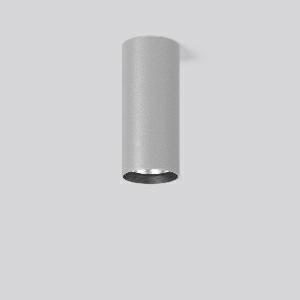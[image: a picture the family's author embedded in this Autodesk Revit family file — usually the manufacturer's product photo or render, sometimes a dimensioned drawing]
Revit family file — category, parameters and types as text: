
# Revit family: heledon_mini_a_931209_004_3_2080
name_source: partatom
category: Lighting Fixtures
units: mm (PartAtom-declared; Revit-internal decimal feet)

## family parameters
Cut with Voids When Loaded = No
Host = Face
Light Source = No
Part Type = Normal
Room Calculation Point = No
Round Connector Dimension = Use Diameter
Shared = No

## types (1)
- HELEDON mini A (1 x LED Modul 935, 3600 lm, 3500)
    Apparent Load = 29 VA
    Approval mark = CE
    CIE Flux Codes = 99 100 100 100 100
    Color Rendering = 92
    Color Temperature = 3500
    Default Elevation = 1800 mm
    Description = Series: HELEDON mini
Cylindrical surface-mounted downlight. Housing: die-cast aluminium, powder-coated. Internal ceiling frame polycarbonate with bayonet mounting. Black plastic ring and recessed LED to prevent glare from the side. Optical assembly with reflector made of MIRO-Silver with 98% total light reflection for outstanding efficiency - can be changed without tools. Best colour rendering index Ra>90. Suitable for Ceiling mounting. Easy installation with a separate ceiling frame with bayonet mounting and plug connection. Driver integrated. Connected via plug-in connector. High quality converter without flickering and stroboscopic effect. The following accessories can be mounted without use of tools: interchangeable lenses, decorative glasses, honeycomb louvre, clear and frosted diffusers, white interchangeable plastic ring. 
Colour: silver
Diameter: 87 mm
Height: 197 mm
Lamp: LED
Socket: without socket
Colour temperature: 3500K
Colour rendering index (CRI): 92
System power: 29 W
Rated luminous flux: 3600 lm
Luminous efficiency: 124 lm/W
Control gear: Regulated power supply
Protection class: I
Type of protection: IP 20
    Height = 197 mm
    Lamp = 1 x LED Modul 935
    Lamp Light Flux = 3600 lm
    Lamp count = 1
    Length = 87 mm
    Lifetime = 50000 h
    Luminous efficacy = 124 lm/W
    Manufacturer = RZB
    ModVariant = No
    Model = 931209.004.3
    Mounting Place = Ceiling
    Mounting Type = Surface mounted
    Number of Poles = 1
    OnlyDefault = Yes
    Power Factor = 1
    Product Name = HELEDON mini A
    Product group = Surface mounted downlights
    ProductGroupID = 302
    Protection Class = Protection class I
    Protection Degree = IP 20
    RLX_Detail_Level = 1
    RLX_Emergency_Light_Flux = 0 lm
    RLX_Emergency_Type = 0
    RLX_Emergency_Type_DB = No
    RlxData = <blob elided: 106029 chars, md5=10737361>
    Socket = socket
    Standby Power = 0 W
    System Light Flux = 3600 lm
    System Power = 29 W
    Type Comments = Product without accessories
    Type Image = 931188.004.jpg
    URL = http://relux.com
    VarID = ---
    Voltage = 230 V
    Voltage Range = 220-240 V
    Weight = 0.00 kg
    Width = 0 mm  [stored 0 ft]

note: [stored X ft] marks values corroborated as IEEE doubles in the binary element streams (Revit-internal decimal feet)

## geometry (parser evidence)
native form markers: Blend x4, Sweep x11
no freeform markers — native parametric forms only
